# Revit family: Gamma-IP30-syst-BE-fr
name_source: partatom
category: Electrical Equipment
units: mm (PartAtom-declared; Revit-internal decimal feet)

## family parameters
Cut with Voids When Loaded = No
Host = Face
Panel Configuration = Two Columns, Circuits Across
Part Type = Panelboard
Room Calculation Point = No
Round Connector Dimension = Use Diameter
Shared = No

## types (4) — shared parameters
EF000003 - mode de pose = EV000384 - saillie
EF000008 - largeur = 250 mm  [stored 0.82021 ft]
EF000049 - profondeur = 103 mm  [stored 0.337927 ft]
EF000116 - numéro RAL = 9010
EF000118 - avec cadre/support de montage = No
EF000339 - type de capot = EV005746 - optionnel
EF001062 - finition CEM = No
EF002950 - largeur en nombre de modules = 13
EF004462 - type de fermeture = EV000154 - autre
EF005474 - indice de protection (IP) = EV006410 - IP30
EF006244 - couvercle/porte transparent(e) = No
EF006306 - avec serrure = No
EF015776 - borne de mise à la terre = No
EF015777 - borne à conducteur neutre = No
EF015941 - porte pour transmission du signal = No
HG000001 - nombre de colonnes = 1
HG000002 - avec porte = No
HG000003 - Gamme = Gamma
HG000005 - Epaisseur = 3 mm  [stored 0.00984252 ft]
HG000006 - encastré = No
HG000009 - Porte à double battant = No
HG000010 - Portes asymétriques = No
HG000011 - Rangées du bas vides = No
Manufacturer = Hager
Type Comments = Gamma
zero-valued in all types: Default Elevation, EF000218 - profondeur d'encastrement, EF000332 - hauteur d'encastrement, EF000846 - largeur d'encastrement, EF001131 - profondeur intérieure, HG000007 - Nombre de colonnes vides, HG000008 - Nombre de rangées vides

## per-type parameters (varying)
| type | EF000007 - couleur | EF000040 - hauteur | EF000266 - nombre de rangées | EF001088 - possibilité de montage en saillie | EF001134 - rail DIN | EF001596 - matériau du boîtier/corps | EF009212 - finition du couvercle | HG000004 - Référence fabricant | Model |
| Saillie IP30 L250 H250 P103 13 Modules - GD113U | 0 | 250 mm  [stored 0.82021 ft] | 1 | No | No | 0 | 0 | GD113U | GD113U |
| Saillie IP30 L250 H375 P103 13 Modules - GD213U | EV000202 - blanc | 375 mm | 2 | Yes | Yes | EV000139 - plastique | EV009916 - avec échancrure | GD213U | GD213U |
| Saillie IP30 L250 H500 P103 13 Modules - GD313U | EV000202 - blanc | 500 mm  [stored 1.64042 ft] | 3 | Yes | Yes | EV000139 - plastique | EV009916 - avec échancrure | GD313U | GD313U |
| Saillie IP30 L250 H625 P103 13 Modules - GD413U | 0 | 625 mm  [stored 2.05052 ft] | 4 | No | No | 0 | 0 | GD413U | GD413U |

note: [stored X ft] marks values corroborated as IEEE doubles in the binary element streams (Revit-internal decimal feet)

## geometry (parser evidence)
native form markers: Sweep x13
no freeform markers — native parametric forms only
